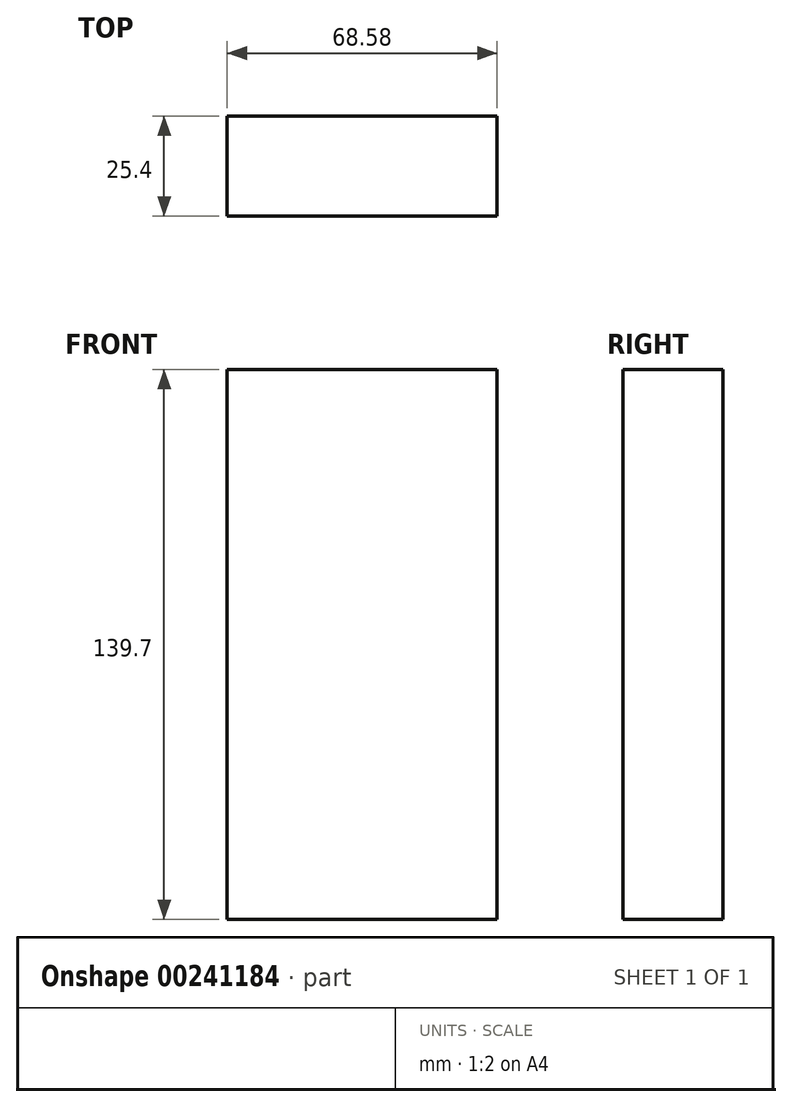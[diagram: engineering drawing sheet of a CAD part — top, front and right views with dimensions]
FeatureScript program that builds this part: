
annotation { "Feature Type Name" : "Feature", "Feature Type Description" : "" }
export const myFeature = defineFeature(function(context is Context, id is Id, definition is map)
    precondition{}
    {
        {
            var Q0;
            Q0=qCreatedBy(makeId("Front.planeOp"),FACE);
            var sketch = newSketch(context, id + "F0", { "sketchPlane" : qUnion([Q0])});
            skLineSegment(sketch, "E0.bottom", {"start": v(34.29, 69.85) * mm, "end": v(-34.3, 69.85) * mm});
            skLineSegment(sketch, "E0.top", {"start": v(34.3, -69.85) * mm, "end": v(-34.29, -69.85) * mm});
            skLineSegment(sketch, "E0.left", {"start": v(34.29, 69.85) * mm, "end": v(34.3, -69.85) * mm});
            skLineSegment(sketch, "E0.right", {"start": v(-34.3, 69.85) * mm, "end": v(-34.29, -69.85) * mm});
            skPoint(sketch, "E0.middle", {"position": v(0, 0) * mm});
            skSolve(sketch);
        }
        {
            var Q0;
            Q0=makeQuery(id+"F0.imprint","IMPRINT",FACE,{"disambiguationData":[TD([[makeQuery(id+"F0.imprint","IMPRINT",EDGE,{"derivedFrom":sQuery(id+"F0.wireOp",EDGE,"E0.bottom")}),1.0]])]});
            extrude(context, id + "F1", {"entities" : qUnion([Q0]), "depth" : 25.4 * mm});
        }
    });
